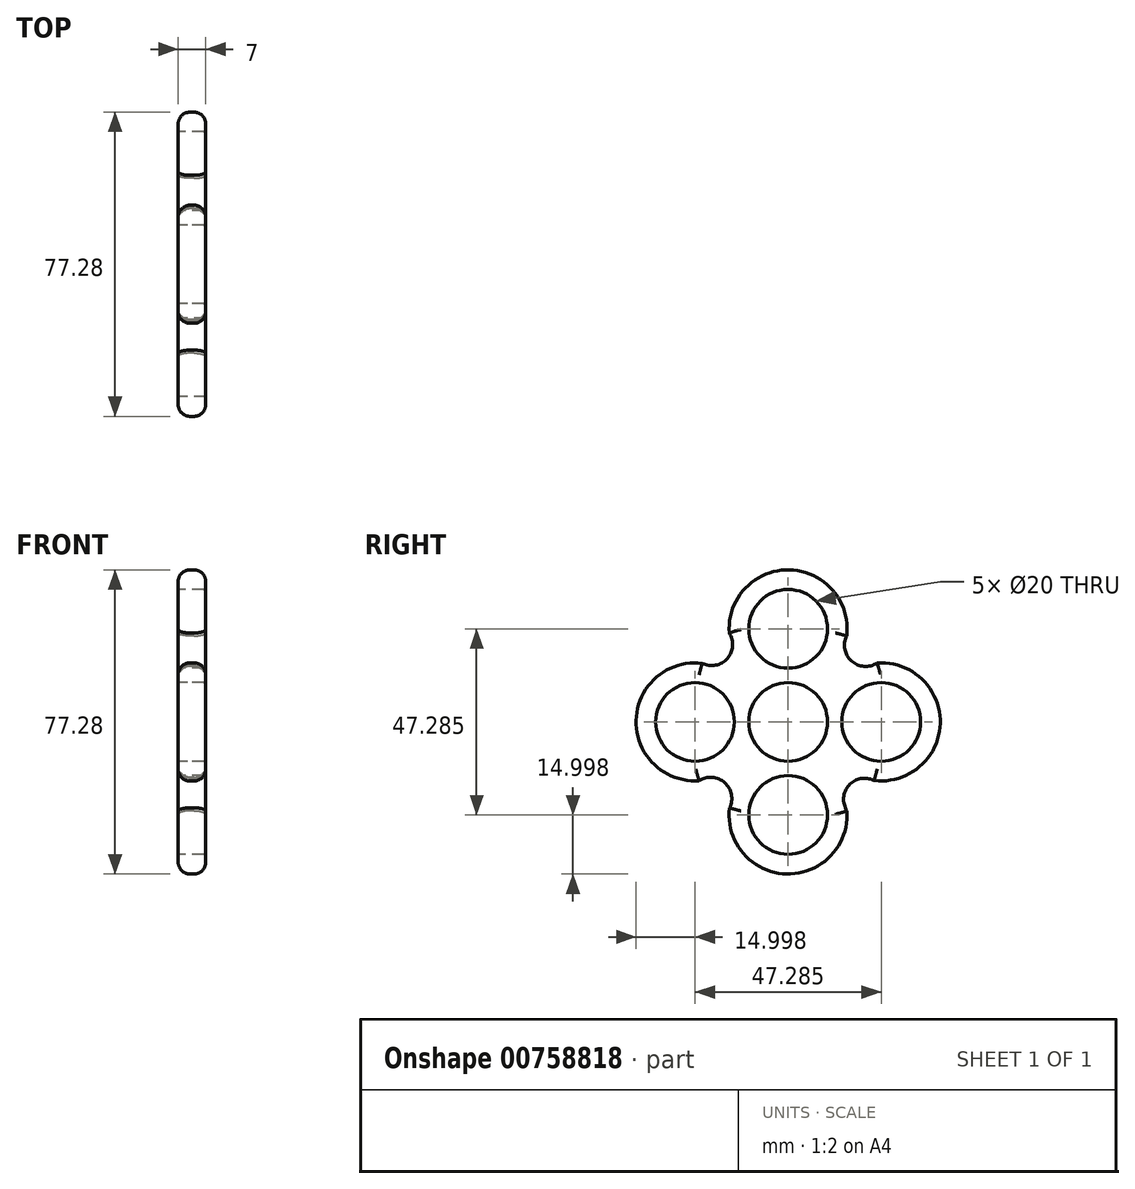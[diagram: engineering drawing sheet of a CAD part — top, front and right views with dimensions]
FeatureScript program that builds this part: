
annotation { "Feature Type Name" : "Feature", "Feature Type Description" : "" }
export const myFeature = defineFeature(function(context is Context, id is Id, definition is map)
    precondition{}
    {
        {
            var Q0;
            Q0=qCreatedBy(makeId("Right.planeOp"),FACE);
            var sketch = newSketch(context, id + "F0", { "sketchPlane" : qUnion([Q0])});
            skPoint(sketch, "E0.center", {"position": v(0, 0) * mm});
            skCircle(sketch, "E1", {"center": v(0, 23.64) * mm, "radius": 15 * mm});
            skCircle(sketch, "E2.1.0", {"center": v(-23.64, 0) * mm, "radius": 15 * mm});
            skCircle(sketch, "E2.2.0", {"center": v(0, -23.64) * mm, "radius": 15 * mm});
            skCircle(sketch, "E2.3.0", {"center": v(23.64, 0) * mm, "radius": 15 * mm});
            skArc(sketch, "E3", {"start": v(14.9, 21.83) * mm, "mid": v(16.1, 15.45) * mm, "end": v(22.6, 14.96) * mm});
            skArc(sketch, "E4.1.0", {"start": v(-21.83, 14.9) * mm, "mid": v(-15.45, 16.1) * mm, "end": v(-14.96, 22.6) * mm});
            skArc(sketch, "E4.2.0", {"start": v(-14.9, -21.83) * mm, "mid": v(-16.1, -15.45) * mm, "end": v(-22.6, -14.96) * mm});
            skArc(sketch, "E4.3.0", {"start": v(21.83, -14.9) * mm, "mid": v(15.45, -16.1) * mm, "end": v(14.96, -22.6) * mm});
            skCircle(sketch, "E5", {"center": v(0, -23.64) * mm, "radius": 10 * mm});
            skCircle(sketch, "E6.1.0", {"center": v(23.64, 0) * mm, "radius": 10 * mm});
            skCircle(sketch, "E6.2.0", {"center": v(0, 23.64) * mm, "radius": 10 * mm});
            skCircle(sketch, "E6.3.0", {"center": v(-23.64, 0) * mm, "radius": 10 * mm});
            skSolve(sketch);
        }
        {
            var Q0;
            {var subQ0=sQuery(id+"F0.wireOp",EDGE,"E4.2.0");var subQ1=sQuery(id+"F0.wireOp",EDGE,"E2.1.0");var subQ2=makeQuery(id+"F0.imprint","INTERSECT",VERTEX,{"disambiguationData":[OD(1.0)],"derivedFrom":[subQ1,subQ0]});Q0=makeQuery(id+"F0.imprint","IMPRINT",FACE,{"disambiguationData":[TD([[makeQuery(id+"F0.imprint","IMPRINT",EDGE,{"disambiguationData":[TD([[subQ2,-1.0]])],"derivedFrom":subQ1}),1.0]])]});}
            var Q1;
            {var subQ0=sQuery(id+"F0.wireOp",EDGE,"E4.1.0");var subQ1=sQuery(id+"F0.wireOp",EDGE,"E1");var subQ2=makeQuery(id+"F0.imprint","INTERSECT",VERTEX,{"disambiguationData":[OD(1.0)],"derivedFrom":[subQ1,subQ0]});Q1=makeQuery(id+"F0.imprint","IMPRINT",FACE,{"disambiguationData":[TD([[makeQuery(id+"F0.imprint","IMPRINT",EDGE,{"disambiguationData":[TD([[subQ2,-1.0]])],"derivedFrom":subQ1}),1.0]])]});}
            var Q2;
            {var subQ9=sQuery(id+"F0.wireOp",EDGE,"E4.1.0");var subQ10=sQuery(id+"F0.wireOp",EDGE,"E1");var subQ11=makeQuery(id+"F0.imprint","INTERSECT",VERTEX,{"disambiguationData":[OD(1.0)],"derivedFrom":[subQ10,subQ9]});Q2=makeQuery(id+"F0.imprint","IMPRINT",FACE,{"disambiguationData":[TD([[makeQuery(id+"F0.imprint","IMPRINT",EDGE,{"disambiguationData":[TD([[subQ11,-1.0]])],"derivedFrom":subQ10}),-1.0]])]});}
            var Q3;
            {var subQ0=sQuery(id+"F0.wireOp",EDGE,"E3");var subQ1=sQuery(id+"F0.wireOp",EDGE,"E2.3.0");var subQ2=makeQuery(id+"F0.imprint","INTERSECT",VERTEX,{"disambiguationData":[OD(1.0)],"derivedFrom":[subQ1,subQ0]});Q3=makeQuery(id+"F0.imprint","IMPRINT",FACE,{"disambiguationData":[TD([[makeQuery(id+"F0.imprint","IMPRINT",EDGE,{"disambiguationData":[TD([[subQ2,-1.0]])],"derivedFrom":subQ1}),1.0]])]});}
            var Q4;
            {var subQ0=sQuery(id+"F0.wireOp",EDGE,"E4.3.0");var subQ1=sQuery(id+"F0.wireOp",EDGE,"E2.2.0");var subQ2=makeQuery(id+"F0.imprint","INTERSECT",VERTEX,{"disambiguationData":[OD(1.0)],"derivedFrom":[subQ1,subQ0]});Q4=makeQuery(id+"F0.imprint","IMPRINT",FACE,{"disambiguationData":[TD([[makeQuery(id+"F0.imprint","IMPRINT",EDGE,{"disambiguationData":[TD([[subQ2,-1.0]])],"derivedFrom":subQ1}),1.0]])]});}
            extrude(context, id + "F1", {"entities" : qUnion([Q0, Q1, Q2, Q3, Q4]), "depth" : 7 * mm, "offsetDistance" : 25.4 * mm});
        }
        {
            var Q0;
            Q0=makeQuery(id+"F1.opExtrude","CAP_EDGE",EDGE,{"disambiguationData":[OSD([sQuery(id+"F0.wireOp",EDGE,"E1")])],"isStart":false});
            var Q1;
            Q1=makeQuery(id+"F1.opExtrude","CAP_EDGE",EDGE,{"disambiguationData":[OSD([sQuery(id+"F0.wireOp",EDGE,"E4.1.0")])],"isStart":false});
            var Q2;
            Q2=makeQuery(id+"F1.opExtrude","CAP_EDGE",EDGE,{"disambiguationData":[OSD([sQuery(id+"F0.wireOp",EDGE,"E2.1.0")])],"isStart":false});
            var Q3;
            Q3=makeQuery(id+"F1.opExtrude","CAP_EDGE",EDGE,{"disambiguationData":[OSD([sQuery(id+"F0.wireOp",EDGE,"E4.2.0")])],"isStart":false});
            var Q4;
            Q4=makeQuery(id+"F1.opExtrude","CAP_EDGE",EDGE,{"disambiguationData":[OSD([sQuery(id+"F0.wireOp",EDGE,"E2.2.0")])],"isStart":false});
            var Q5;
            Q5=makeQuery(id+"F1.opExtrude","CAP_EDGE",EDGE,{"disambiguationData":[OSD([sQuery(id+"F0.wireOp",EDGE,"E3")])],"isStart":false});
            var Q6;
            Q6=makeQuery(id+"F1.opExtrude","CAP_EDGE",EDGE,{"disambiguationData":[OSD([sQuery(id+"F0.wireOp",EDGE,"E2.3.0")])],"isStart":false});
            var Q7;
            Q7=makeQuery(id+"F1.opExtrude","CAP_EDGE",EDGE,{"disambiguationData":[OSD([sQuery(id+"F0.wireOp",EDGE,"E4.3.0")])],"isStart":false});
            var Q8;
            Q8=makeQuery(id+"F1.opExtrude","CAP_EDGE",EDGE,{"disambiguationData":[OSD([sQuery(id+"F0.wireOp",EDGE,"E2.1.0")])],"isStart":true});
            var Q9;
            Q9=makeQuery(id+"F1.opExtrude","CAP_EDGE",EDGE,{"disambiguationData":[OSD([sQuery(id+"F0.wireOp",EDGE,"E4.2.0")])],"isStart":true});
            var Q10;
            Q10=makeQuery(id+"F1.opExtrude","CAP_EDGE",EDGE,{"disambiguationData":[OSD([sQuery(id+"F0.wireOp",EDGE,"E2.2.0")])],"isStart":true});
            var Q11;
            Q11=makeQuery(id+"F1.opExtrude","CAP_EDGE",EDGE,{"disambiguationData":[OSD([sQuery(id+"F0.wireOp",EDGE,"E4.3.0")])],"isStart":true});
            var Q12;
            Q12=makeQuery(id+"F1.opExtrude","CAP_EDGE",EDGE,{"disambiguationData":[OSD([sQuery(id+"F0.wireOp",EDGE,"E2.3.0")])],"isStart":true});
            var Q13;
            Q13=makeQuery(id+"F1.opExtrude","CAP_EDGE",EDGE,{"disambiguationData":[OSD([sQuery(id+"F0.wireOp",EDGE,"E3")])],"isStart":true});
            var Q14;
            Q14=makeQuery(id+"F1.opExtrude","CAP_EDGE",EDGE,{"disambiguationData":[OSD([sQuery(id+"F0.wireOp",EDGE,"E1")])],"isStart":true});
            var Q15;
            Q15=makeQuery(id+"F1.opExtrude","CAP_EDGE",EDGE,{"disambiguationData":[OSD([sQuery(id+"F0.wireOp",EDGE,"E4.1.0")])],"isStart":true});
            fillet(context, id + "F2", {"entities" : qUnion([Q0, Q1, Q2, Q3, Q4, Q5, Q6, Q7, Q8, Q9, Q10, Q11, Q12, Q13, Q14, Q15]), "radius" : 3 * mm, "tangentPropagation" : true, "allowEdgeOverflow" : false});
        }
        {
            var Q0;
            Q0=qCreatedBy(makeId("Right.planeOp"),FACE);
            var sketch = newSketch(context, id + "F3", { "sketchPlane" : qUnion([Q0])});
            skCircle(sketch, "E7", {"center": v(0, 0) * mm, "radius": 10 * mm});
            skSolve(sketch);
        }
        {
            var Q0;
            Q0=makeQuery(id+"F3.imprint","IMPRINT",FACE,{"disambiguationData":[TD([[makeQuery(id+"F3.imprint","IMPRINT",EDGE,{"derivedFrom":sQuery(id+"F3.wireOp",EDGE,"E7")}),1.0]])]});
            extrude(context, id + "F4", {"entities" : qUnion([Q0]), "operationType" : NewBodyOperationType.REMOVE, "oppositeDirection" : true, "depth" : -7 * mm, "offsetDistance" : 25.4 * mm});
        }
        {
            var Q0;
            Q0=makeQuery(id+"F1.opExtrude","CAP_EDGE",EDGE,{"disambiguationData":[OSD([sQuery(id+"F0.wireOp",EDGE,"E6.1.0")])],"isStart":true});
            var Q1;
            Q1=makeQuery(id+"F1.opExtrude","CAP_EDGE",EDGE,{"disambiguationData":[OSD([sQuery(id+"F0.wireOp",EDGE,"E6.2.0")])],"isStart":true});
            var Q2;
            Q2=makeQuery(id+"F4.boolean.opBoolean","COPY",EDGE,{"derivedFrom":makeQuery(id+"F4.opExtrude","CAP_EDGE",EDGE,{"disambiguationData":[OSD([sQuery(id+"F3.wireOp",EDGE,"E7")])],"isStart":true})});
            var Q3;
            Q3=makeQuery(id+"F1.opExtrude","CAP_EDGE",EDGE,{"disambiguationData":[OSD([sQuery(id+"F0.wireOp",EDGE,"E6.3.0")])],"isStart":true});
            var Q4;
            Q4=makeQuery(id+"F1.opExtrude","CAP_EDGE",EDGE,{"disambiguationData":[OSD([sQuery(id+"F0.wireOp",EDGE,"E5")])],"isStart":true});
            var Q5;
            Q5=makeQuery(id+"F1.opExtrude","CAP_EDGE",EDGE,{"disambiguationData":[OSD([sQuery(id+"F0.wireOp",EDGE,"E6.1.0")])],"isStart":false});
            var Q6;
            Q6=makeQuery(id+"F1.opExtrude","CAP_EDGE",EDGE,{"disambiguationData":[OSD([sQuery(id+"F0.wireOp",EDGE,"E6.2.0")])],"isStart":false});
            var Q7;
            Q7=makeQuery(id+"F4.boolean.opBoolean","COPY",EDGE,{"derivedFrom":makeQuery(id+"F4.opExtrude","CAP_EDGE",EDGE,{"disambiguationData":[OSD([sQuery(id+"F3.wireOp",EDGE,"E7")])],"isStart":false})});
            var Q8;
            Q8=makeQuery(id+"F1.opExtrude","CAP_EDGE",EDGE,{"disambiguationData":[OSD([sQuery(id+"F0.wireOp",EDGE,"E5")])],"isStart":false});
            fillet(context, id + "F5", {"entities" : qUnion([Q0, Q1, Q2, Q3, Q4, Q5, Q6, Q7, Q8]), "radius" : .5 * mm, "tangentPropagation" : true, "allowEdgeOverflow" : false});
        }
    });
